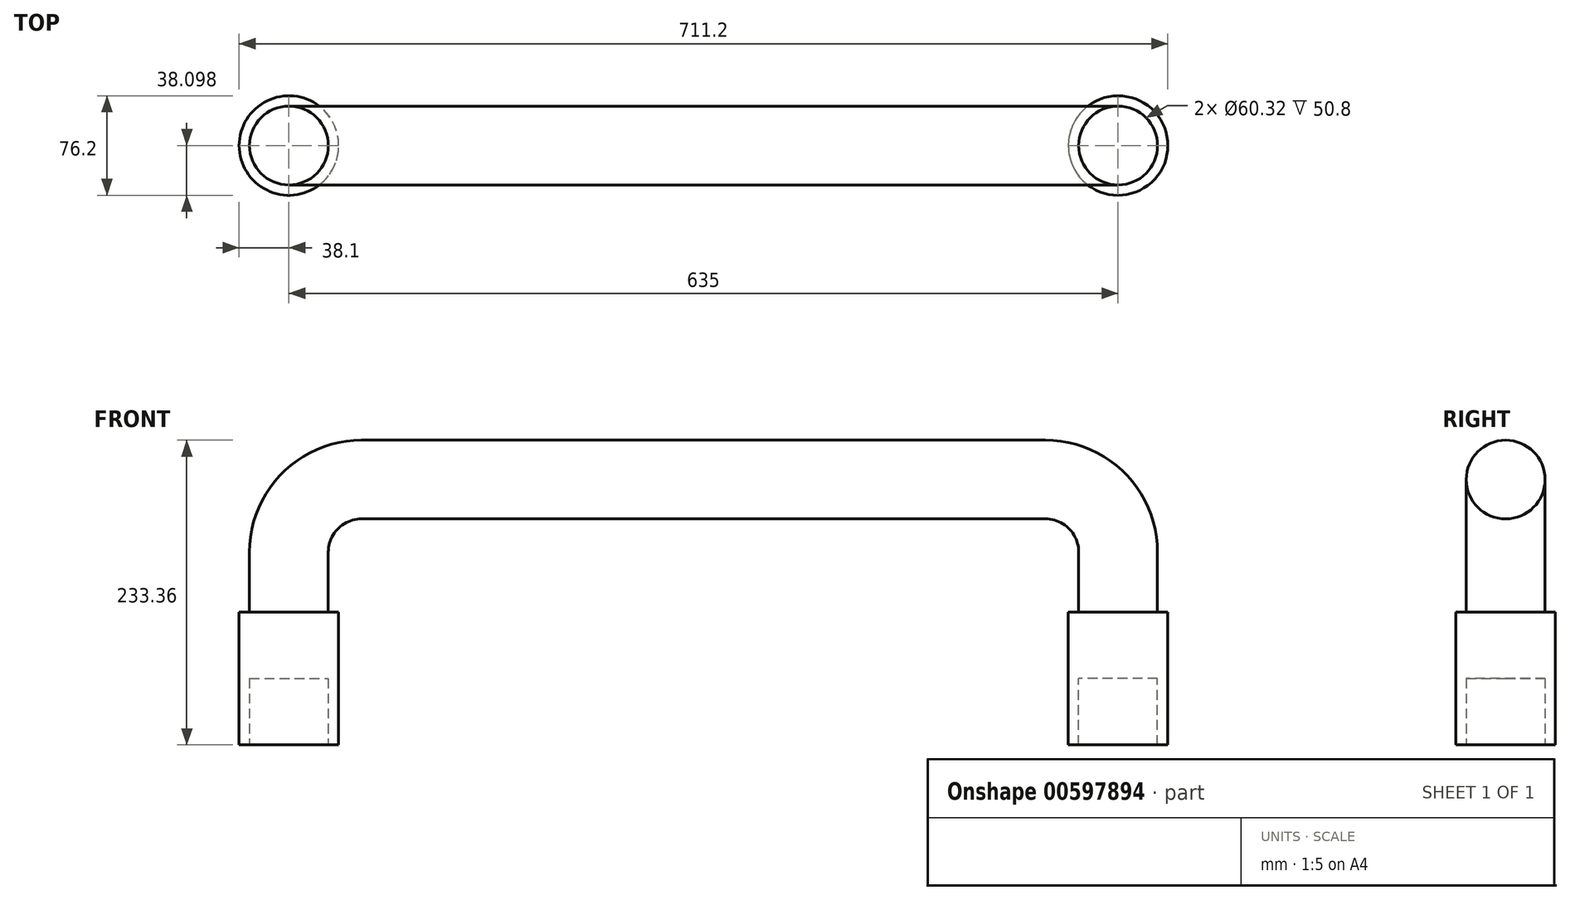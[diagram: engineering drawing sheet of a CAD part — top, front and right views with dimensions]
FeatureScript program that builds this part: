
annotation { "Feature Type Name" : "Feature", "Feature Type Description" : "" }
export const myFeature = defineFeature(function(context is Context, id is Id, definition is map)
    precondition{}
    {
        {
            var Q0;
            Q0=qCreatedBy(makeId("Front.planeOp"),FACE);
            var sketch = newSketch(context, id + "F0", { "sketchPlane" : qUnion([Q0])});
            skLineSegment(sketch, "E0", {"start": v(0, 0) * mm, "end": v(-317.5, 0) * mm, "construction": true});
            skLineSegment(sketch, "E1", {"start": v(0, 0) * mm, "end": v(317.5, 0) * mm, "construction": true});
            skLineSegment(sketch, "E2", {"start": v(-317.5, 0) * mm, "end": v(-317.5, 114.3) * mm});
            skLineSegment(sketch, "E3", {"start": v(-279.4, 152.4) * mm, "end": v(292.1, 152.4) * mm});
            skLineSegment(sketch, "E4", {"start": v(317.5, 127) * mm, "end": v(317.5, 0) * mm});
            skPoint(sketch, "E5.visualSharp", {"position": v(-317.5, 152.4) * mm});
            skPoint(sketch, "E6.visualSharp", {"position": v(317.5, 152.4) * mm});
            skLineSegment(sketch, "E7", {"start": v(-317.5, 0) * mm, "end": v(-347.66, 0) * mm});
            skLineSegment(sketch, "E8", {"start": v(-347.66, 0) * mm, "end": v(-347.66, 96.84) * mm});
            skLineSegment(sketch, "E9", {"start": v(-261.94, 182.56) * mm, "end": v(261.94, 182.56) * mm});
            skLineSegment(sketch, "E10", {"start": v(347.66, 96.84) * mm, "end": v(347.66, 0) * mm});
            skLineSegment(sketch, "E11", {"start": v(347.66, 0) * mm, "end": v(317.5, 0) * mm});
            skPoint(sketch, "E12.visualSharp", {"position": v(-347.66, 182.56) * mm});
            skArc(sketch, "E12.filletArc", {"start": v(-261.94, 182.56) * mm, "mid": v(-322.55, 157.45) * mm, "end": v(-347.66, 96.84) * mm});
            skPoint(sketch, "E13.visualSharp", {"position": v(347.66, 182.56) * mm});
            skArc(sketch, "E13.filletArc", {"start": v(347.66, 96.84) * mm, "mid": v(322.55, 157.45) * mm, "end": v(261.94, 182.56) * mm});
            skLineSegment(sketch, "E14", {"start": v(-317.5, 0) * mm, "end": v(-287.34, 0) * mm});
            skLineSegment(sketch, "E15", {"start": v(-287.34, 0) * mm, "end": v(-287.34, 96.84) * mm});
            skLineSegment(sketch, "E16", {"start": v(-261.94, 122.24) * mm, "end": v(261.94, 122.24) * mm});
            skLineSegment(sketch, "E17", {"start": v(287.34, 96.84) * mm, "end": v(287.34, 0) * mm});
            skLineSegment(sketch, "E18", {"start": v(287.34, 0) * mm, "end": v(317.5, 0) * mm});
            skPoint(sketch, "E19.visualSharp", {"position": v(-287.34, 122.24) * mm});
            skArc(sketch, "E19.filletArc", {"start": v(-261.94, 122.24) * mm, "mid": v(-279.9, 114.8) * mm, "end": v(-287.34, 96.84) * mm});
            skArc(sketch, "E20.filletArc", {"start": v(287.34, 96.84) * mm, "mid": v(279.9, 114.8) * mm, "end": v(261.94, 122.24) * mm});
            skPoint(sketch, "E21.middle", {"position": v(-317.5, 34.93) * mm});
            skPoint(sketch, "E22.middle", {"position": v(317.5, 34.92) * mm});
            skSolve(sketch);
        }
        {
            var Q0;
            Q0 = qSketchRegion(id + "F0", true);
            extrude(context, id + "F1", {"entities" : qUnion([Q0]), "depth" : 60.32 * mm, "offsetDistance" : 25.4 * mm});
        }
        {
            var Q0;
            Q0=makeQuery(id+"F1.opExtrude","CAP_EDGE",EDGE,{"disambiguationData":[OSD([sQuery(id+"F0.wireOp",EDGE,"E9")])],"isStart":false});
            var Q1;
            Q1=makeQuery(id+"F1.opExtrude","CAP_EDGE",EDGE,{"disambiguationData":[OSD([sQuery(id+"F0.wireOp",EDGE,"E16")])],"isStart":false});
            var Q2;
            Q2=makeQuery(id+"F1.opExtrude","CAP_EDGE",EDGE,{"disambiguationData":[OSD([sQuery(id+"F0.wireOp",EDGE,"E9")])],"isStart":true});
            var Q3;
            Q3=makeQuery(id+"F1.opExtrude","CAP_EDGE",EDGE,{"disambiguationData":[OSD([sQuery(id+"F0.wireOp",EDGE,"E16")])],"isStart":true});
            fillet(context, id + "F2", {"entities" : qUnion([Q0, Q1, Q2, Q3]), "radius" : 30.16 * mm, "tangentPropagation" : true, "allowEdgeOverflow" : false});
        }
        {
            var Q0;
            Q0=makeQuery(id+"F1.opExtrude","SWEPT_FACE",FACE,{"disambiguationData":[OSD([sQuery(id+"F0.wireOp",EDGE,"E7"),sQuery(id+"F0.wireOp",EDGE,"E14")])]});
            var sketch = newSketch(context, id + "F3", { "sketchPlane" : qUnion([Q0])});
            skCircle(sketch, "E23", {"center": v(-317.5, 30.16) * mm, "radius": 30.16 * mm});
            skCircle(sketch, "E24", {"center": v(-317.5, 30.16) * mm, "radius": 38.1 * mm});
            skSolve(sketch);
        }
        {
            var Q0;
            Q0 = qSketchRegion(id + "F3", true);
            extrude(context, id + "F4", {"entities" : qUnion([Q0]), "operationType" : NewBodyOperationType.ADD, "oppositeDirection" : true, "depth" : 101.6 * mm, "offsetDistance" : 25.4 * mm, "symmetric" : true});
        }
        {
            var Q0;
            Q0=makeQuery(id+"F1.opExtrude","SWEPT_FACE",FACE,{"disambiguationData":[OSD([sQuery(id+"F0.wireOp",EDGE,"E11"),sQuery(id+"F0.wireOp",EDGE,"E18")])]});
            var sketch = newSketch(context, id + "F5", { "sketchPlane" : qUnion([Q0])});
            skCircle(sketch, "E25", {"center": v(317.5, 30.16) * mm, "radius": 30.16 * mm});
            skCircle(sketch, "E26", {"center": v(317.5, 30.16) * mm, "radius": 38.1 * mm});
            skSolve(sketch);
        }
        {
            var Q0;
            Q0 = qSketchRegion(id + "F5", true);
            extrude(context, id + "F6", {"entities" : qUnion([Q0]), "operationType" : NewBodyOperationType.ADD, "depth" : 101.6 * mm, "offsetDistance" : 25.4 * mm, "symmetric" : true});
        }
    });
